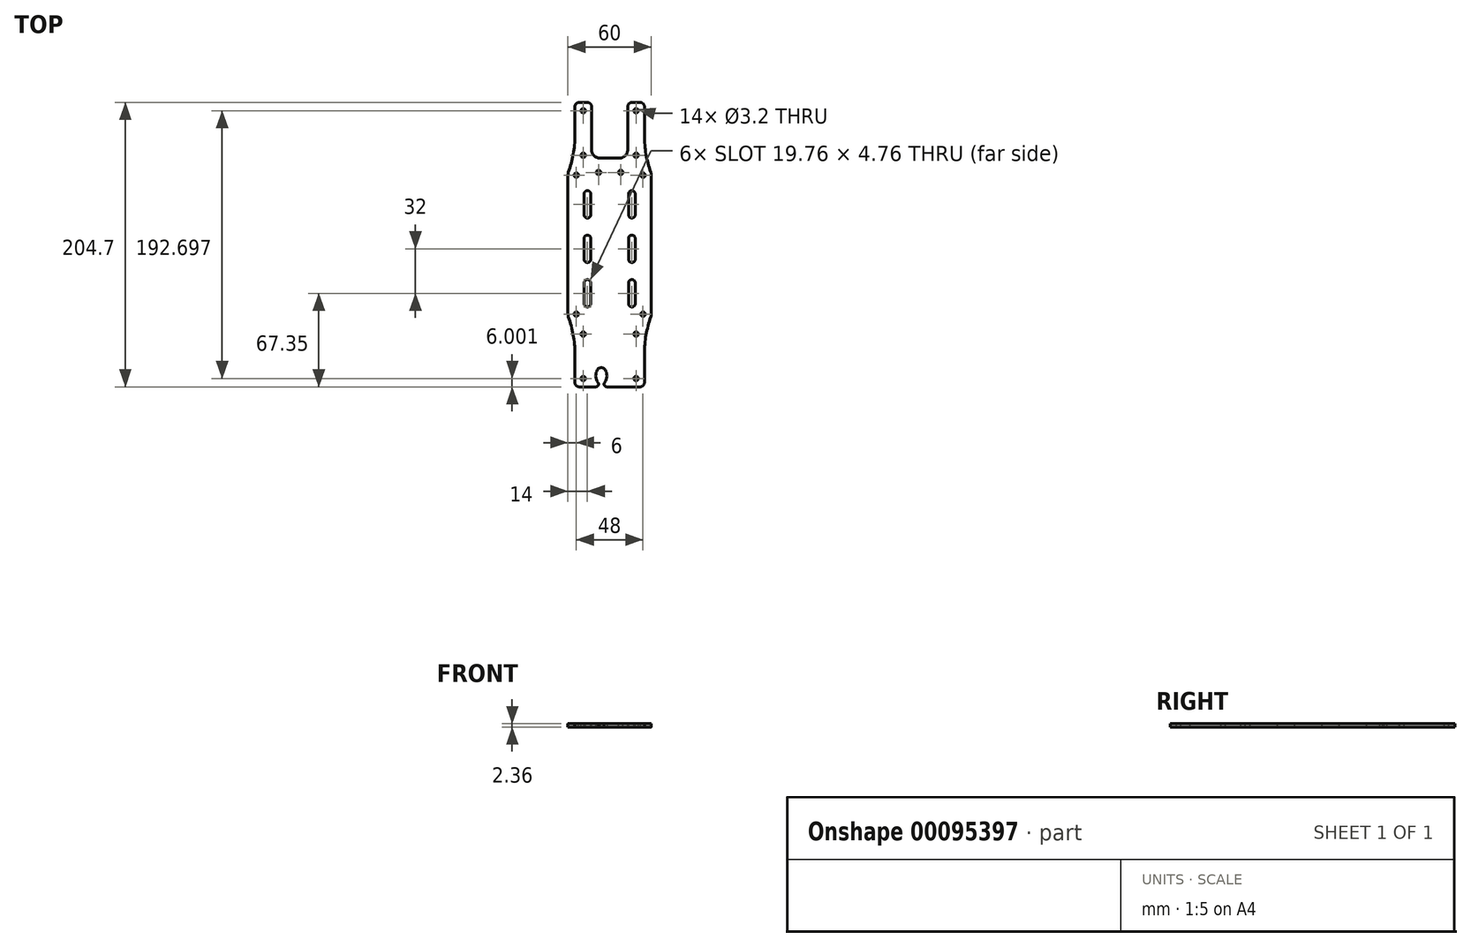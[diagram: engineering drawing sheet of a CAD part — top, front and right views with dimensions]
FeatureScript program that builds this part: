
annotation { "Feature Type Name" : "Feature", "Feature Type Description" : "" }
export const myFeature = defineFeature(function(context is Context, id is Id, definition is map)
    precondition{}
    {
        {
            var Q0;
            Q0=qCreatedBy(makeId("Top.planeOp"),FACE);
            var sketch = newSketch(context, id + "F0", { "sketchPlane" : qUnion([Q0])});
            skLineSegment(sketch, "E0", {"start": v(0, 102.35) * mm, "end": v(-22, 102.35) * mm});
            skLineSegment(sketch, "E1", {"start": v(-25, 99.35) * mm, "end": v(-25, 78.35) * mm});
            skLineSegment(sketch, "E2", {"start": v(-22, -102.35) * mm, "end": v(0, -102.35) * mm});
            skArc(sketch, "E3.filletArc", {"start": v(-22, 102.35) * mm, "mid": v(-24.12, 101.47) * mm, "end": v(-25, 99.35) * mm});
            skArc(sketch, "E4.filletArc", {"start": v(-25, -99.35) * mm, "mid": v(-24.12, -101.47) * mm, "end": v(-22, -102.35) * mm});
            skArc(sketch, "E5.filletArc", {"start": v(-29.64, 52.05) * mm, "mid": v(-29.9, 51.04) * mm, "end": v(-30, 50) * mm});
            skArc(sketch, "E6.MirrorCS", {"start": v(-29.64, -52.05) * mm, "mid": v(-29.9, -51.04) * mm, "end": v(-30, -50) * mm});
            skLineSegment(sketch, "E7.trimOffspring", {"start": v(-25, -78.35) * mm, "end": v(-25, -99.35) * mm});
            skArc(sketch, "E8", {"start": v(-25, -78.35) * mm, "mid": v(-26.17, -65) * mm, "end": v(-29.64, -52.05) * mm});
            skArc(sketch, "E9", {"start": v(-29.64, 52.05) * mm, "mid": v(-26.17, 65) * mm, "end": v(-25, 78.35) * mm});
            skCircle(sketch, "E10", {"center": v(0, 0) * mm, "radius": 125 * mm, "construction": true});
            skLineSegment(sketch, "E11", {"start": v(-95.76, 80.35) * mm, "end": v(95.76, -80.35) * mm, "construction": true});
            skLineSegment(sketch, "E12", {"start": v(95.76, 80.35) * mm, "end": v(-95.76, -80.35) * mm, "construction": true});
            skLineSegment(sketch, "E13", {"start": v(0, 125) * mm, "end": v(0, -125) * mm, "construction": true});
            skLineSegment(sketch, "E14", {"start": v(-95.76, 80.35) * mm, "end": v(95.76, 80.35) * mm, "construction": true});
            skLineSegment(sketch, "E15", {"start": v(-95.76, -80.35) * mm, "end": v(95.76, -80.35) * mm, "construction": true});
            skLineSegment(sketch, "E16", {"start": v(-30, 50) * mm, "end": v(-30, -50) * mm});
            skLineSegment(sketch, "E17.MirrorCS", {"start": v(0, 102.35) * mm, "end": v(22, 102.35) * mm});
            skArc(sketch, "E18.MirrorCS", {"start": v(22, 102.35) * mm, "mid": v(24.12, 101.47) * mm, "end": v(25, 99.35) * mm});
            skLineSegment(sketch, "E19.MirrorCS", {"start": v(25, 99.35) * mm, "end": v(25, 78.35) * mm});
            skArc(sketch, "E20.MirrorCS", {"start": v(29.64, 52.05) * mm, "mid": v(26.17, 65) * mm, "end": v(25, 78.35) * mm});
            skArc(sketch, "E21.MirrorCS", {"start": v(29.64, 52.05) * mm, "mid": v(29.9, 51.04) * mm, "end": v(30, 50) * mm});
            skLineSegment(sketch, "E22.MirrorCS", {"start": v(30, 50) * mm, "end": v(30, -50) * mm});
            skArc(sketch, "E23.MirrorCS", {"start": v(29.64, -52.05) * mm, "mid": v(29.9, -51.04) * mm, "end": v(30, -50) * mm});
            skArc(sketch, "E24.MirrorCS", {"start": v(25, -78.35) * mm, "mid": v(26.17, -65) * mm, "end": v(29.64, -52.05) * mm});
            skArc(sketch, "E25.MirrorCS", {"start": v(25, -99.35) * mm, "mid": v(24.12, -101.47) * mm, "end": v(22, -102.35) * mm});
            skLineSegment(sketch, "E26.MirrorCS", {"start": v(22, -102.35) * mm, "end": v(0, -102.35) * mm});
            skLineSegment(sketch, "E27.MirrorCS", {"start": v(25, -78.35) * mm, "end": v(25, -99.35) * mm});
            skSolve(sketch);
        }
        {
            var Q0;
            Q0=qSketchRegion(id+"F0",true);
            extrude(context, id + "F1", {"entities" : qUnion([Q0]), "oppositeDirection" : true, "depth" : 2.36 * mm});
        }
        {
            var Q0;
            Q0=makeQuery(id+"F1.opExtrude","CAP_FACE",FACE,{"disambiguationData":[OSD([sQuery(id+"F0.wireOp",EDGE,"E0"),sQuery(id+"F0.wireOp",EDGE,"E1"),sQuery(id+"F0.wireOp",EDGE,"E2"),sQuery(id+"F0.wireOp",EDGE,"E3.filletArc"),sQuery(id+"F0.wireOp",EDGE,"E4.filletArc"),sQuery(id+"F0.wireOp",EDGE,"d22b67ea-32aa-4b1a-bfbd-94ae52c1f5b30.MirrorCS"),sQuery(id+"F0.wireOp",EDGE,"d22b67ea-32aa-4b1a-bfbd-94ae52c1f5b31.MirrorCS"),sQuery(id+"F0.wireOp",EDGE,"d22b67ea-32aa-4b1a-bfbd-94ae52c1f5b32.MirrorCS"),sQuery(id+"F0.wireOp",EDGE,"d22b67ea-32aa-4b1a-bfbd-94ae52c1f5b33.MirrorCS"),sQuery(id+"F0.wireOp",EDGE,"d22b67ea-32aa-4b1a-bfbd-94ae52c1f5b34.MirrorCS")])],"isStart":true});
            var sketch = newSketch(context, id + "F2", { "sketchPlane" : qUnion([Q0])});
            skCircle(sketch, "E28", {"center": v(-19, 96.35) * mm, "radius": 1.6 * mm});
            skCircle(sketch, "E29", {"center": v(-19, 64.35) * mm, "radius": 1.6 * mm});
            skCircle(sketch, "E30", {"center": v(-19, -96.35) * mm, "radius": 1.6 * mm});
            skCircle(sketch, "E31", {"center": v(-19, -64.35) * mm, "radius": 1.6 * mm});
            skCircle(sketch, "E32", {"center": v(-24, -50) * mm, "radius": 1.6 * mm});
            skCircle(sketch, "E33", {"center": v(-24, 50) * mm, "radius": 1.6 * mm});
            skLineSegment(sketch, "E34", {"start": v(-19, 96.35) * mm, "end": v(-19, -96.35) * mm, "construction": true});
            skCircle(sketch, "E35.MirrorC", {"center": v(19, 96.35) * mm, "radius": 1.6 * mm});
            skCircle(sketch, "E36.MirrorC", {"center": v(19, 64.35) * mm, "radius": 1.6 * mm});
            skCircle(sketch, "E37.MirrorC", {"center": v(24, 50) * mm, "radius": 1.6 * mm});
            skCircle(sketch, "E38.MirrorC", {"center": v(24, -50) * mm, "radius": 1.6 * mm});
            skCircle(sketch, "E39.MirrorC", {"center": v(19, -64.35) * mm, "radius": 1.6 * mm});
            skCircle(sketch, "E40.MirrorC", {"center": v(19, -96.35) * mm, "radius": 1.6 * mm});
            skLineSegment(sketch, "E41", {"start": v(0, 0) * mm, "end": v(-30, 0) * mm, "construction": true});
            skLineSegment(sketch, "E42.left", {"start": v(-13.62, -42.5) * mm, "end": v(-13.62, -27.5) * mm});
            skLineSegment(sketch, "E42.right", {"start": v(-18.38, -42.5) * mm, "end": v(-18.38, -27.5) * mm});
            skPoint(sketch, "E42.middle", {"position": v(-16, -35) * mm});
            skArc(sketch, "E43", {"start": v(-13.62, -27.5) * mm, "mid": v(-16, -25.12) * mm, "end": v(-18.38, -27.5) * mm});
            skArc(sketch, "E44", {"start": v(-18.38, -42.5) * mm, "mid": v(-16, -44.88) * mm, "end": v(-13.62, -42.5) * mm});
            skArc(sketch, "E45.0.1.0", {"start": v(-18.38, -10.5) * mm, "mid": v(-16, -12.88) * mm, "end": v(-13.62, -10.5) * mm});
            skLineSegment(sketch, "E45.0.1.1", {"start": v(-18.38, -10.5) * mm, "end": v(-18.38, 4.5) * mm});
            skArc(sketch, "E45.0.1.2", {"start": v(-13.62, 4.5) * mm, "mid": v(-16, 6.88) * mm, "end": v(-18.38, 4.5) * mm});
            skLineSegment(sketch, "E45.0.1.3", {"start": v(-13.62, -10.5) * mm, "end": v(-13.62, 4.5) * mm});
            skArc(sketch, "E45.0.2.0", {"start": v(-18.38, 21.5) * mm, "mid": v(-16, 19.12) * mm, "end": v(-13.62, 21.5) * mm});
            skLineSegment(sketch, "E45.0.2.1", {"start": v(-18.38, 21.5) * mm, "end": v(-18.38, 36.5) * mm});
            skArc(sketch, "E45.0.2.2", {"start": v(-13.62, 36.5) * mm, "mid": v(-16, 38.88) * mm, "end": v(-18.38, 36.5) * mm});
            skLineSegment(sketch, "E45.0.2.3", {"start": v(-13.62, 21.5) * mm, "end": v(-13.62, 36.5) * mm});
            skArc(sketch, "E45.1.0.0", {"start": v(13.62, -42.5) * mm, "mid": v(16, -44.88) * mm, "end": v(18.38, -42.5) * mm});
            skLineSegment(sketch, "E45.1.0.1", {"start": v(13.62, -42.5) * mm, "end": v(13.62, -27.5) * mm});
            skArc(sketch, "E45.1.0.2", {"start": v(18.38, -27.5) * mm, "mid": v(16, -25.12) * mm, "end": v(13.62, -27.5) * mm});
            skLineSegment(sketch, "E45.1.0.3", {"start": v(18.38, -42.5) * mm, "end": v(18.38, -27.5) * mm});
            skArc(sketch, "E45.1.1.0", {"start": v(13.62, -10.5) * mm, "mid": v(16, -12.88) * mm, "end": v(18.38, -10.5) * mm});
            skLineSegment(sketch, "E45.1.1.1", {"start": v(13.62, -10.5) * mm, "end": v(13.62, 4.5) * mm});
            skArc(sketch, "E45.1.1.2", {"start": v(18.38, 4.5) * mm, "mid": v(16, 6.88) * mm, "end": v(13.62, 4.5) * mm});
            skLineSegment(sketch, "E45.1.1.3", {"start": v(18.38, -10.5) * mm, "end": v(18.38, 4.5) * mm});
            skArc(sketch, "E45.1.2.0", {"start": v(13.62, 21.5) * mm, "mid": v(16, 19.12) * mm, "end": v(18.38, 21.5) * mm});
            skLineSegment(sketch, "E45.1.2.1", {"start": v(13.62, 21.5) * mm, "end": v(13.62, 36.5) * mm});
            skArc(sketch, "E45.1.2.2", {"start": v(18.38, 36.5) * mm, "mid": v(16, 38.88) * mm, "end": v(13.62, 36.5) * mm});
            skLineSegment(sketch, "E45.1.2.3", {"start": v(18.38, 21.5) * mm, "end": v(18.38, 36.5) * mm});
            skLineSegment(sketch, "E45.direction1", {"start": v(-18.38, -42.5) * mm, "end": v(13.62, -42.5) * mm, "construction": true});
            skLineSegment(sketch, "E45.direction2", {"start": v(-18.38, -42.5) * mm, "end": v(-18.38, -10.5) * mm, "construction": true});
            skLineSegment(sketch, "E46", {"start": v(-8, 52) * mm, "end": v(8, 52) * mm, "construction": true});
            skPoint(sketch, "E47", {"position": v(0, 52) * mm});
            skCircle(sketch, "E48", {"center": v(-8, 52) * mm, "radius": 1.6 * mm});
            skCircle(sketch, "E49", {"center": v(8, 52) * mm, "radius": 1.6 * mm});
            skSolve(sketch);
        }
        {
            var Q0;
            Q0=qSketchRegion(id+"F2",true);
            extrude(context, id + "F3", {"entities" : qUnion([Q0]), "operationType" : NewBodyOperationType.REMOVE, "endBound" : BoundingType.THROUGH_ALL, "oppositeDirection" : true, "depth" : 25.4 * mm});
        }
        {
            var Q0;
            Q0=qCreatedBy(makeId("Top.planeOp"),FACE);
            var sketch = newSketch(context, id + "F4", { "sketchPlane" : qUnion([Q0])});
            skCircle(sketch, "E50.cCircle", {"center": v(-24, 50) * mm, "radius": 3.1 * mm, "construction": true});
            skLineSegment(sketch, "E50.0", {"start": v(-24, 53.58) * mm, "end": v(-20.9, 51.79) * mm, "construction": true});
            skLineSegment(sketch, "E50.1", {"start": v(-20.9, 51.79) * mm, "end": v(-20.9, 48.21) * mm, "construction": true});
            skLineSegment(sketch, "E50.2", {"start": v(-20.9, 48.21) * mm, "end": v(-24, 46.42) * mm, "construction": true});
            skLineSegment(sketch, "E50.3", {"start": v(-24, 46.42) * mm, "end": v(-27.1, 48.21) * mm, "construction": true});
            skLineSegment(sketch, "E50.4", {"start": v(-27.1, 48.21) * mm, "end": v(-27.1, 51.79) * mm, "construction": true});
            skLineSegment(sketch, "E50.5", {"start": v(-27.1, 51.79) * mm, "end": v(-24, 53.58) * mm, "construction": true});
            skPoint(sketch, "E50.0.midPoint", {"position": v(-22.45, 52.68) * mm});
            skArc(sketch, "E51", {"start": v(-20, 45.53) * mm, "mid": v(-24, 56) * mm, "end": v(-28, 45.53) * mm});
            skArc(sketch, "E52", {"start": v(-28, -45.53) * mm, "mid": v(-24, -56) * mm, "end": v(-20, -45.53) * mm});
            skLineSegment(sketch, "E53", {"start": v(-26, 41.06) * mm, "end": v(-26, -41.06) * mm});
            skLineSegment(sketch, "E54", {"start": v(-22, 41.06) * mm, "end": v(-22, -41.06) * mm});
            skPoint(sketch, "E55.visualSharp", {"position": v(-26, 44.34) * mm});
            skArc(sketch, "E55.filletArc", {"start": v(-26, 41.06) * mm, "mid": v(-26.52, 43.5) * mm, "end": v(-28, 45.53) * mm});
            skPoint(sketch, "E56.visualSharp", {"position": v(-22, 44.34) * mm});
            skArc(sketch, "E56.filletArc", {"start": v(-20, 45.53) * mm, "mid": v(-21.48, 43.5) * mm, "end": v(-22, 41.06) * mm});
            skPoint(sketch, "E57.visualSharp", {"position": v(-22, -44.34) * mm});
            skArc(sketch, "E57.filletArc", {"start": v(-22, -41.06) * mm, "mid": v(-21.48, -43.5) * mm, "end": v(-20, -45.53) * mm});
            skPoint(sketch, "E58.visualSharp", {"position": v(-26, -44.34) * mm});
            skArc(sketch, "E58.filletArc", {"start": v(-28, -45.53) * mm, "mid": v(-26.52, -43.5) * mm, "end": v(-26, -41.06) * mm});
            skLineSegment(sketch, "E59", {"start": v(-24, 50) * mm, "end": v(-24, -50) * mm, "construction": true});
            skSolve(sketch);
        }
        {
            var Q0;
            Q0=qSketchRegion(id+"F4",true);
            extrude(context, id + "F5", {"entities" : qUnion([Q0]), "depth" : 25 * mm});
        }
        {
            var Q0;
            Q0=makeQuery(id+"F5.opExtrude","CAP_FACE",FACE,{"disambiguationData":[OSD([sQuery(id+"F4.wireOp",EDGE,"E51"),sQuery(id+"F4.wireOp",EDGE,"E52"),sQuery(id+"F4.wireOp",EDGE,"E53"),sQuery(id+"F4.wireOp",EDGE,"E54"),sQuery(id+"F4.wireOp",EDGE,"E55.filletArc"),sQuery(id+"F4.wireOp",EDGE,"E56.filletArc"),sQuery(id+"F4.wireOp",EDGE,"E57.filletArc"),sQuery(id+"F4.wireOp",EDGE,"E58.filletArc")])],"isStart":true});
            var sketch = newSketch(context, id + "F6", { "sketchPlane" : qUnion([Q0])});
            skCircle(sketch, "E60.cCircle", {"center": v(-24, -50) * mm, "radius": 3.05 * mm, "construction": true});
            skLineSegment(sketch, "E60.0", {"start": v(-27.05, -48.24) * mm, "end": v(-24, -46.48) * mm});
            skLineSegment(sketch, "E60.1", {"start": v(-24, -46.48) * mm, "end": v(-20.95, -48.24) * mm});
            skLineSegment(sketch, "E60.2", {"start": v(-20.95, -48.24) * mm, "end": v(-20.95, -51.76) * mm});
            skLineSegment(sketch, "E60.3", {"start": v(-20.95, -51.76) * mm, "end": v(-24, -53.52) * mm});
            skLineSegment(sketch, "E60.4", {"start": v(-24, -53.52) * mm, "end": v(-27.05, -51.76) * mm});
            skLineSegment(sketch, "E60.5", {"start": v(-27.05, -51.76) * mm, "end": v(-27.05, -48.24) * mm});
            skPoint(sketch, "E60.0.midPoint", {"position": v(-25.53, -47.36) * mm});
            skCircle(sketch, "E61.cCircle", {"center": v(-24, 50) * mm, "radius": 3.05 * mm, "construction": true});
            skLineSegment(sketch, "E61.0", {"start": v(-27.05, 51.76) * mm, "end": v(-24, 53.52) * mm});
            skLineSegment(sketch, "E61.1", {"start": v(-24, 53.52) * mm, "end": v(-20.95, 51.76) * mm});
            skLineSegment(sketch, "E61.2", {"start": v(-20.95, 51.76) * mm, "end": v(-20.95, 48.24) * mm});
            skLineSegment(sketch, "E61.3", {"start": v(-20.95, 48.24) * mm, "end": v(-24, 46.48) * mm});
            skLineSegment(sketch, "E61.4", {"start": v(-24, 46.48) * mm, "end": v(-27.05, 48.24) * mm});
            skLineSegment(sketch, "E61.5", {"start": v(-27.05, 48.24) * mm, "end": v(-27.05, 51.76) * mm});
            skPoint(sketch, "E61.0.midPoint", {"position": v(-25.52, 52.64) * mm});
            skSolve(sketch);
        }
        {
            var Q0;
            Q0=qSketchRegion(id+"F6",true);
            var Q1;
            Q1=makeQuery(id+"F5.opExtrude","CAP_FACE",FACE,{"disambiguationData":[OSD([sQuery(id+"F4.wireOp",EDGE,"E51"),sQuery(id+"F4.wireOp",EDGE,"E52"),sQuery(id+"F4.wireOp",EDGE,"E53"),sQuery(id+"F4.wireOp",EDGE,"E54"),sQuery(id+"F4.wireOp",EDGE,"E55.filletArc"),sQuery(id+"F4.wireOp",EDGE,"E56.filletArc"),sQuery(id+"F4.wireOp",EDGE,"E57.filletArc"),sQuery(id+"F4.wireOp",EDGE,"E58.filletArc")])],"isStart":false});
            extrude(context, id + "F7", {"entities" : qUnion([Q0]), "operationType" : NewBodyOperationType.REMOVE, "endBound" : BoundingType.UP_TO_SURFACE, "oppositeDirection" : true, "endBoundEntityFace" : qUnion([Q1]), "depth" : 25 * mm});
        }
        {
            var Q0;
            Q0=makeQuery(id+"F5.opExtrude","SWEPT_FACE",FACE,{"disambiguationData":[OSD([sQuery(id+"F4.wireOp",EDGE,"E53")])]});
            var sketch = newSketch(context, id + "F8", { "sketchPlane" : qUnion([Q0])});
            skLineSegment(sketch, "E62", {"start": v(-21.13, 12.5) * mm, "end": v(21.13, 12.5) * mm, "construction": true});
            skLineSegment(sketch, "E63.bottom", {"start": v(-11.25, 17.5) * mm, "end": v(-19.25, 17.5) * mm});
            skLineSegment(sketch, "E63.top", {"start": v(-11.25, 7.5) * mm, "end": v(-19.25, 7.5) * mm});
            skLineSegment(sketch, "E63.left", {"start": v(-10.25, 16.5) * mm, "end": v(-10.25, 8.5) * mm});
            skLineSegment(sketch, "E63.right", {"start": v(-20.25, 16.5) * mm, "end": v(-20.25, 8.5) * mm});
            skPoint(sketch, "E63.middle", {"position": v(-15.25, 12.5) * mm});
            skPoint(sketch, "E64.visualSharp", {"position": v(-20.25, 17.5) * mm});
            skArc(sketch, "E64.filletArc", {"start": v(-19.25, 17.5) * mm, "mid": v(-19.96, 17.2) * mm, "end": v(-20.25, 16.5) * mm});
            skPoint(sketch, "E65.visualSharp", {"position": v(-20.25, 7.5) * mm});
            skArc(sketch, "E65.filletArc", {"start": v(-20.25, 8.5) * mm, "mid": v(-19.96, 7.8) * mm, "end": v(-19.25, 7.5) * mm});
            skPoint(sketch, "E66.visualSharp", {"position": v(-10.25, 7.5) * mm});
            skArc(sketch, "E66.filletArc", {"start": v(-11.25, 7.5) * mm, "mid": v(-10.54, 7.8) * mm, "end": v(-10.25, 8.5) * mm});
            skPoint(sketch, "E67.visualSharp", {"position": v(-10.25, 17.5) * mm});
            skArc(sketch, "E67.filletArc", {"start": v(-10.25, 16.5) * mm, "mid": v(-10.54, 17.2) * mm, "end": v(-11.25, 17.5) * mm});
            skLineSegment(sketch, "E68.bottom", {"start": v(-7.5, 0) * mm, "end": v(7.5, 0) * mm});
            skLineSegment(sketch, "E68.top", {"start": v(-6.5, 3.5) * mm, "end": v(6.5, 3.5) * mm});
            skLineSegment(sketch, "E68.left", {"start": v(-7.5, 0) * mm, "end": v(-7.5, 2.5) * mm});
            skLineSegment(sketch, "E68.right", {"start": v(7.5, 0) * mm, "end": v(7.5, 2.5) * mm});
            skPoint(sketch, "E69.visualSharp", {"position": v(-7.5, 3.5) * mm});
            skArc(sketch, "E69.filletArc", {"start": v(-6.5, 3.5) * mm, "mid": v(-7.2, 3.2) * mm, "end": v(-7.5, 2.5) * mm});
            skPoint(sketch, "E70.visualSharp", {"position": v(7.5, 3.5) * mm});
            skArc(sketch, "E70.filletArc", {"start": v(7.5, 2.5) * mm, "mid": v(7.2, 3.2) * mm, "end": v(6.5, 3.5) * mm});
            skArc(sketch, "E71", {"start": v(-27, 25) * mm, "mid": v(-25, 23) * mm, "end": v(-23, 25) * mm});
            skLineSegment(sketch, "E72", {"start": v(-25, 25) * mm, "end": v(-25, 0) * mm, "construction": true});
            skArc(sketch, "E73", {"start": v(-23, 0) * mm, "mid": v(-25, 2) * mm, "end": v(-27, 0) * mm});
            skLineSegment(sketch, "E74", {"start": v(-27, 25) * mm, "end": v(-23, 25) * mm});
            skLineSegment(sketch, "E75", {"start": v(-27, 0) * mm, "end": v(-23, 0) * mm});
            skLineSegment(sketch, "E76", {"start": v(0, 25) * mm, "end": v(0, 0) * mm, "construction": true});
            skPoint(sketch, "E77", {"position": v(0, 12.5) * mm});
            skArc(sketch, "E78.MirrorCS", {"start": v(11.25, 7.5) * mm, "mid": v(10.54, 7.8) * mm, "end": v(10.25, 8.5) * mm});
            skArc(sketch, "E79.MirrorCS", {"start": v(10.25, 16.5) * mm, "mid": v(10.54, 17.2) * mm, "end": v(11.25, 17.5) * mm});
            skArc(sketch, "E80.MirrorCS", {"start": v(20.25, 8.5) * mm, "mid": v(19.96, 7.8) * mm, "end": v(19.25, 7.5) * mm});
            skArc(sketch, "E81.MirrorCS", {"start": v(19.25, 17.5) * mm, "mid": v(19.96, 17.2) * mm, "end": v(20.25, 16.5) * mm});
            skPoint(sketch, "E82.MirrorP", {"position": v(10.25, 17.5) * mm});
            skLineSegment(sketch, "E83.MirrorCS", {"start": v(20.25, 16.5) * mm, "end": v(20.25, 8.5) * mm});
            skLineSegment(sketch, "E84.MirrorCS", {"start": v(10.25, 16.5) * mm, "end": v(10.25, 8.5) * mm});
            skLineSegment(sketch, "E85.MirrorCS", {"start": v(11.25, 17.5) * mm, "end": v(19.25, 17.5) * mm});
            skLineSegment(sketch, "E86.MirrorCS", {"start": v(11.25, 7.5) * mm, "end": v(19.25, 7.5) * mm});
            skPoint(sketch, "E87.MirrorP", {"position": v(20.25, 7.5) * mm});
            skPoint(sketch, "E88.MirrorP", {"position": v(15.25, 12.5) * mm});
            skPoint(sketch, "E89.MirrorP", {"position": v(20.25, 17.5) * mm});
            skPoint(sketch, "E90.MirrorP", {"position": v(10.25, 7.5) * mm});
            skLineSegment(sketch, "E91.MirrorCS", {"start": v(27, 25) * mm, "end": v(23, 25) * mm});
            skLineSegment(sketch, "E92.MirrorCS", {"start": v(25, 25) * mm, "end": v(25, 0) * mm, "construction": true});
            skArc(sketch, "E93.MirrorCS", {"start": v(27, 25) * mm, "mid": v(25, 23) * mm, "end": v(23, 25) * mm});
            skLineSegment(sketch, "E94.MirrorCS", {"start": v(27, 0) * mm, "end": v(23, 0) * mm});
            skArc(sketch, "E95.MirrorCS", {"start": v(23, 0) * mm, "mid": v(25, 2) * mm, "end": v(27, 0) * mm});
            skArc(sketch, "E96.MirrorCS", {"start": v(-6.5, 21.5) * mm, "mid": v(-7.2, 21.8) * mm, "end": v(-7.5, 22.5) * mm});
            skArc(sketch, "E97.MirrorCS", {"start": v(7.5, 22.5) * mm, "mid": v(7.2, 21.8) * mm, "end": v(6.5, 21.5) * mm});
            skPoint(sketch, "E98.MirrorP", {"position": v(-7.5, 21.5) * mm});
            skLineSegment(sketch, "E99.MirrorCS", {"start": v(-6.5, 21.5) * mm, "end": v(6.5, 21.5) * mm});
            skLineSegment(sketch, "E100.MirrorCS", {"start": v(-7.5, 25) * mm, "end": v(-7.5, 22.5) * mm});
            skPoint(sketch, "E101.MirrorP", {"position": v(7.5, 21.5) * mm});
            skLineSegment(sketch, "E102.MirrorCS", {"start": v(7.5, 25) * mm, "end": v(7.5, 22.5) * mm});
            skLineSegment(sketch, "E103.MirrorCS", {"start": v(-7.5, 25) * mm, "end": v(7.5, 25) * mm});
            skSolve(sketch);
        }
        {
            var Q0;
            Q0=qSketchRegion(id+"F8",true);
            var Q1;
            Q1=makeQuery(id+"F5.opExtrude","SWEPT_FACE",FACE,{"disambiguationData":[OSD([sQuery(id+"F4.wireOp",EDGE,"E54")])]});
            extrude(context, id + "F9", {"entities" : qUnion([Q0]), "operationType" : NewBodyOperationType.REMOVE, "endBound" : BoundingType.UP_TO_SURFACE, "oppositeDirection" : true, "endBoundEntityFace" : qUnion([Q1]), "depth" : 25 * mm});
        }
        {
            var Q0;
            Q0=qCreatedBy(makeId("Top.planeOp"),FACE);
            cPlane(context, id + "F10", {"entities" : qUnion([Q0]), "cplaneType" : CPlaneType.OFFSET, "offset" : 12.5 * mm, "width" : 150 * mm, "height" : 150 * mm});
        }
        {
            var Q0;
            Q0=qCreatedBy(id+"F10.planeOp",FACE);
            var sketch = newSketch(context, id + "F11", { "sketchPlane" : qUnion([Q0])});
            skLineSegment(sketch, "E104", {"start": v(-26.25, 21.25) * mm, "end": v(-26.25, 19.75) * mm});
            skLineSegment(sketch, "E105", {"start": v(-25.75, 19.25) * mm, "end": v(-19.25, 19.25) * mm});
            skLineSegment(sketch, "E106", {"start": v(-19.25, 19.25) * mm, "end": v(-18.25, 18.25) * mm});
            skLineSegment(sketch, "E107", {"start": v(-18.25, 18.25) * mm, "end": v(-15.25, 18.25) * mm});
            skLineSegment(sketch, "E108", {"start": v(-6.48, 15.25) * mm, "end": v(-35.06, 15.25) * mm, "construction": true});
            skArc(sketch, "E109", {"start": v(-12.25, 15.25) * mm, "mid": v(-13.13, 17.37) * mm, "end": v(-15.25, 18.25) * mm});
            skLineSegment(sketch, "E110", {"start": v(-26.25, 21.25) * mm, "end": v(-27.75, 21.25) * mm});
            skLineSegment(sketch, "E111", {"start": v(-27.75, 21.25) * mm, "end": v(-27.75, 15.25) * mm});
            skPoint(sketch, "E112.visualSharp", {"position": v(-26.25, 19.25) * mm});
            skArc(sketch, "E112.filletArc", {"start": v(-26.25, 19.75) * mm, "mid": v(-26.1, 19.4) * mm, "end": v(-25.75, 19.25) * mm});
            skLineSegment(sketch, "E113.MirrorCS", {"start": v(-27.75, 9.25) * mm, "end": v(-27.75, 15.25) * mm});
            skLineSegment(sketch, "E114.MirrorCS", {"start": v(-26.25, 9.25) * mm, "end": v(-27.75, 9.25) * mm});
            skLineSegment(sketch, "E115.MirrorCS", {"start": v(-26.25, 9.25) * mm, "end": v(-26.25, 10.75) * mm});
            skArc(sketch, "E116.MirrorCS", {"start": v(-26.25, 10.75) * mm, "mid": v(-26.1, 11.1) * mm, "end": v(-25.75, 11.25) * mm});
            skLineSegment(sketch, "E117.MirrorCS", {"start": v(-25.75, 11.25) * mm, "end": v(-19.25, 11.25) * mm});
            skLineSegment(sketch, "E118.MirrorCS", {"start": v(-19.25, 11.25) * mm, "end": v(-18.25, 12.25) * mm});
            skLineSegment(sketch, "E119.MirrorCS", {"start": v(-18.25, 12.25) * mm, "end": v(-15.25, 12.25) * mm});
            skArc(sketch, "E120.MirrorCS", {"start": v(-12.25, 15.25) * mm, "mid": v(-13.13, 13.13) * mm, "end": v(-15.25, 12.25) * mm});
            skSolve(sketch);
        }
        {
            var Q0;
            Q0=qSketchRegion(id+"F11",true);
            extrude(context, id + "F12", {"entities" : qUnion([Q0]), "endBound" : BoundingType.SYMMETRIC, "depth" : 8 * mm});
        }
        {
            var Q0;
            Q0=makeQuery(id+"F12.opExtrude","CAP_FACE",FACE,{"disambiguationData":[OSD([sQuery(id+"F11.wireOp",EDGE,"E104"),sQuery(id+"F11.wireOp",EDGE,"E105"),sQuery(id+"F11.wireOp",EDGE,"E106"),sQuery(id+"F11.wireOp",EDGE,"E107"),sQuery(id+"F11.wireOp",EDGE,"E109"),sQuery(id+"F11.wireOp",EDGE,"E110"),sQuery(id+"F11.wireOp",EDGE,"E111"),sQuery(id+"F11.wireOp",EDGE,"E112.filletArc"),sQuery(id+"F11.wireOp",EDGE,"E113.MirrorCS"),sQuery(id+"F11.wireOp",EDGE,"E114.MirrorCS"),sQuery(id+"F11.wireOp",EDGE,"E115.MirrorCS"),sQuery(id+"F11.wireOp",EDGE,"E116.MirrorCS"),sQuery(id+"F11.wireOp",EDGE,"E117.MirrorCS"),sQuery(id+"F11.wireOp",EDGE,"E118.MirrorCS"),sQuery(id+"F11.wireOp",EDGE,"E119.MirrorCS"),sQuery(id+"F11.wireOp",EDGE,"E120.MirrorCS")])],"isStart":false});
            var sketch = newSketch(context, id + "F13", { "sketchPlane" : qUnion([Q0])});
            skCircle(sketch, "E121", {"center": v(-15.25, 15.25) * mm, "radius": 1.5 * mm});
            skSolve(sketch);
        }
        {
            var Q0;
            Q0=qSketchRegion(id+"F13",true);
            var Q1;
            Q1=makeQuery(id+"F12.opExtrude","CAP_FACE",FACE,{"disambiguationData":[OSD([sQuery(id+"F11.wireOp",EDGE,"E104"),sQuery(id+"F11.wireOp",EDGE,"E105"),sQuery(id+"F11.wireOp",EDGE,"E106"),sQuery(id+"F11.wireOp",EDGE,"E107"),sQuery(id+"F11.wireOp",EDGE,"E109"),sQuery(id+"F11.wireOp",EDGE,"E110"),sQuery(id+"F11.wireOp",EDGE,"E111"),sQuery(id+"F11.wireOp",EDGE,"E112.filletArc"),sQuery(id+"F11.wireOp",EDGE,"E113.MirrorCS"),sQuery(id+"F11.wireOp",EDGE,"E114.MirrorCS"),sQuery(id+"F11.wireOp",EDGE,"E115.MirrorCS"),sQuery(id+"F11.wireOp",EDGE,"E116.MirrorCS"),sQuery(id+"F11.wireOp",EDGE,"E117.MirrorCS"),sQuery(id+"F11.wireOp",EDGE,"E118.MirrorCS"),sQuery(id+"F11.wireOp",EDGE,"E119.MirrorCS"),sQuery(id+"F11.wireOp",EDGE,"E120.MirrorCS")])],"isStart":true});
            extrude(context, id + "F14", {"entities" : qUnion([Q0]), "operationType" : NewBodyOperationType.REMOVE, "endBound" : BoundingType.UP_TO_SURFACE, "oppositeDirection" : true, "endBoundEntityFace" : qUnion([Q1]), "depth" : 25 * mm});
        }
        {
            var Q0;
            Q0=makeQuery(id+"F5.opExtrude","SWEPT_BODY",BODY,{"disambiguationData":[OSD([sQuery(id+"F4.wireOp",EDGE,"E51"),sQuery(id+"F4.wireOp",EDGE,"E52"),sQuery(id+"F4.wireOp",EDGE,"E53"),sQuery(id+"F4.wireOp",EDGE,"E54"),sQuery(id+"F4.wireOp",EDGE,"E55.filletArc"),sQuery(id+"F4.wireOp",EDGE,"E56.filletArc"),sQuery(id+"F4.wireOp",EDGE,"E57.filletArc"),sQuery(id+"F4.wireOp",EDGE,"E58.filletArc")])]});
            deleteBodies(context, id + "F15", {"entities" : qUnion([Q0])});
        }
        {
            var Q0;
            Q0=makeQuery(id+"F12.opExtrude","SWEPT_BODY",BODY,{"disambiguationData":[OSD([sQuery(id+"F11.wireOp",EDGE,"E104"),sQuery(id+"F11.wireOp",EDGE,"E105"),sQuery(id+"F11.wireOp",EDGE,"E106"),sQuery(id+"F11.wireOp",EDGE,"E107"),sQuery(id+"F11.wireOp",EDGE,"E109"),sQuery(id+"F11.wireOp",EDGE,"E110"),sQuery(id+"F11.wireOp",EDGE,"E111"),sQuery(id+"F11.wireOp",EDGE,"E112.filletArc"),sQuery(id+"F11.wireOp",EDGE,"E113.MirrorCS"),sQuery(id+"F11.wireOp",EDGE,"E114.MirrorCS"),sQuery(id+"F11.wireOp",EDGE,"E115.MirrorCS"),sQuery(id+"F11.wireOp",EDGE,"E116.MirrorCS"),sQuery(id+"F11.wireOp",EDGE,"E117.MirrorCS"),sQuery(id+"F11.wireOp",EDGE,"E118.MirrorCS"),sQuery(id+"F11.wireOp",EDGE,"E119.MirrorCS"),sQuery(id+"F11.wireOp",EDGE,"E120.MirrorCS")])]});
            deleteBodies(context, id + "F16", {"entities" : qUnion([Q0])});
        }
        {
            var Q0;
            Q0=makeQuery(id+"F0.imprint","IMPRINT",FACE,{"disambiguationData":[TD([[makeQuery(id+"F0.imprint","IMPRINT",EDGE,{"derivedFrom":sQuery(id+"F0.wireOp",EDGE,"E0")}),1.0]])]});
            var sketch = newSketch(context, id + "F17", { "sketchPlane" : qUnion([Q0])});
            skLineSegment(sketch, "E122", {"start": v(0, 62.35) * mm, "end": v(-7, 62.35) * mm});
            skLineSegment(sketch, "E123", {"start": v(-13, 68.35) * mm, "end": v(-13, 99.35) * mm});
            skLineSegment(sketch, "E124", {"start": v(-16, 102.35) * mm, "end": v(-16, 102.35) * mm});
            skLineSegment(sketch, "E125", {"start": v(-16, 102.35) * mm, "end": v(-16, 105.35) * mm});
            skLineSegment(sketch, "E126", {"start": v(-16, 105.35) * mm, "end": v(0, 105.35) * mm});
            skPoint(sketch, "E127.visualSharp", {"position": v(-13, 62.35) * mm});
            skArc(sketch, "E127.filletArc", {"start": v(-13, 68.35) * mm, "mid": v(-11.24, 64.1) * mm, "end": v(-7, 62.35) * mm});
            skPoint(sketch, "E128.visualSharp", {"position": v(-13, 102.35) * mm});
            skArc(sketch, "E128.filletArc", {"start": v(-13, 99.35) * mm, "mid": v(-13.88, 101.47) * mm, "end": v(-16, 102.35) * mm});
            skLineSegment(sketch, "E129.MirrorCS", {"start": v(16, 102.35) * mm, "end": v(16, 105.35) * mm});
            skArc(sketch, "E130.MirrorCS", {"start": v(13, 99.35) * mm, "mid": v(13.88, 101.47) * mm, "end": v(16, 102.35) * mm});
            skArc(sketch, "E131.MirrorCS", {"start": v(13, 68.35) * mm, "mid": v(11.24, 64.1) * mm, "end": v(7, 62.35) * mm});
            skPoint(sketch, "E132.MirrorP", {"position": v(13, 102.35) * mm});
            skPoint(sketch, "E133.MirrorP", {"position": v(13, 62.35) * mm});
            skLineSegment(sketch, "E134.MirrorCS", {"start": v(16, 105.35) * mm, "end": v(0, 105.35) * mm});
            skLineSegment(sketch, "E135.MirrorCS", {"start": v(0, 62.35) * mm, "end": v(7, 62.35) * mm});
            skLineSegment(sketch, "E136.MirrorCS", {"start": v(13, 68.35) * mm, "end": v(13, 99.35) * mm});
            skSolve(sketch);
        }
        {
            var Q0;
            Q0 = qSketchRegion(id + "F17", true);
            var Q1;
            Q1=makeQuery(id+"F1.opExtrude","CAP_FACE",FACE,{"disambiguationData":[OSD([sQuery(id+"F0.wireOp",EDGE,"E0"),sQuery(id+"F0.wireOp",EDGE,"E1"),sQuery(id+"F0.wireOp",EDGE,"E2"),sQuery(id+"F0.wireOp",EDGE,"E3.filletArc"),sQuery(id+"F0.wireOp",EDGE,"E4.filletArc"),sQuery(id+"F0.wireOp",EDGE,"E5.filletArc"),sQuery(id+"F0.wireOp",EDGE,"E6.MirrorCS"),sQuery(id+"F0.wireOp",EDGE,"E7.trimOffspring"),sQuery(id+"F0.wireOp",EDGE,"E8"),sQuery(id+"F0.wireOp",EDGE,"E9"),sQuery(id+"F0.wireOp",EDGE,"E16"),sQuery(id+"F0.wireOp",EDGE,"E17.MirrorCS"),sQuery(id+"F0.wireOp",EDGE,"E18.MirrorCS"),sQuery(id+"F0.wireOp",EDGE,"E19.MirrorCS"),sQuery(id+"F0.wireOp",EDGE,"E20.MirrorCS"),sQuery(id+"F0.wireOp",EDGE,"E21.MirrorCS"),sQuery(id+"F0.wireOp",EDGE,"E22.MirrorCS"),sQuery(id+"F0.wireOp",EDGE,"E23.MirrorCS"),sQuery(id+"F0.wireOp",EDGE,"E24.MirrorCS"),sQuery(id+"F0.wireOp",EDGE,"E25.MirrorCS"),sQuery(id+"F0.wireOp",EDGE,"E26.MirrorCS"),sQuery(id+"F0.wireOp",EDGE,"E27.MirrorCS")])],"isStart":false});
            extrude(context, id + "F18", {"entities" : qUnion([Q0]), "operationType" : NewBodyOperationType.REMOVE, "endBound" : BoundingType.UP_TO_SURFACE, "oppositeDirection" : true, "endBoundEntityFace" : qUnion([Q1]), "depth" : 25 * mm});
        }
        {
            var Q0;
            Q0=makeQuery(id+"F1.opExtrude","CAP_FACE",FACE,{"disambiguationData":[OSD([sQuery(id+"F0.wireOp",EDGE,"E0"),sQuery(id+"F0.wireOp",EDGE,"E1"),sQuery(id+"F0.wireOp",EDGE,"E2"),sQuery(id+"F0.wireOp",EDGE,"E3.filletArc"),sQuery(id+"F0.wireOp",EDGE,"E4.filletArc"),sQuery(id+"F0.wireOp",EDGE,"E5.filletArc"),sQuery(id+"F0.wireOp",EDGE,"E6.MirrorCS"),sQuery(id+"F0.wireOp",EDGE,"E7.trimOffspring"),sQuery(id+"F0.wireOp",EDGE,"E8"),sQuery(id+"F0.wireOp",EDGE,"E9"),sQuery(id+"F0.wireOp",EDGE,"E16"),sQuery(id+"F0.wireOp",EDGE,"E17.MirrorCS"),sQuery(id+"F0.wireOp",EDGE,"E18.MirrorCS"),sQuery(id+"F0.wireOp",EDGE,"E19.MirrorCS"),sQuery(id+"F0.wireOp",EDGE,"E20.MirrorCS"),sQuery(id+"F0.wireOp",EDGE,"E21.MirrorCS"),sQuery(id+"F0.wireOp",EDGE,"E22.MirrorCS"),sQuery(id+"F0.wireOp",EDGE,"E23.MirrorCS"),sQuery(id+"F0.wireOp",EDGE,"E24.MirrorCS"),sQuery(id+"F0.wireOp",EDGE,"E25.MirrorCS"),sQuery(id+"F0.wireOp",EDGE,"E26.MirrorCS"),sQuery(id+"F0.wireOp",EDGE,"E27.MirrorCS")])],"isStart":true});
            var sketch = newSketch(context, id + "F19", { "sketchPlane" : qUnion([Q0])});
            skEllipticalArc(sketch, "E137", {});
            skArc(sketch, "E138", {"start": v(-10, -102.35) * mm, "mid": v(-8.19, -101.2) * mm, "end": v(-8.48, -99.06) * mm});
            skLineSegment(sketch, "E139", {"start": v(-6, -94.35) * mm, "end": v(-6, -104.97) * mm, "construction": true});
            skArc(sketch, "E140.MirrorCS", {"start": v(-2, -102.35) * mm, "mid": v(-3.81, -101.2) * mm, "end": v(-3.52, -99.06) * mm});
            skLineSegment(sketch, "E141", {"start": v(-10, -102.35) * mm, "end": v(-10, -103.35) * mm});
            skLineSegment(sketch, "E142", {"start": v(-10, -103.35) * mm, "end": v(-2, -103.35) * mm});
            skLineSegment(sketch, "E143", {"start": v(-2, -103.35) * mm, "end": v(-2, -102.35) * mm});
            const initialGuessF19  = {"E137": [-0.006, -0.09434845121081742, 0, 1, 0.006, 0.004, 3.808895997013649, 2.474289310165937]};
            skSetInitialGuess(sketch, initialGuessF19);
            skSolve(sketch);
        }
        {
            var Q0;
            Q0 = qSketchRegion(id + "F19", true);
            var Q1;
            Q1=makeQuery(id+"F1.opExtrude","CAP_FACE",FACE,{"disambiguationData":[OSD([sQuery(id+"F0.wireOp",EDGE,"E0"),sQuery(id+"F0.wireOp",EDGE,"E1"),sQuery(id+"F0.wireOp",EDGE,"E2"),sQuery(id+"F0.wireOp",EDGE,"E3.filletArc"),sQuery(id+"F0.wireOp",EDGE,"E4.filletArc"),sQuery(id+"F0.wireOp",EDGE,"E5.filletArc"),sQuery(id+"F0.wireOp",EDGE,"E6.MirrorCS"),sQuery(id+"F0.wireOp",EDGE,"E7.trimOffspring"),sQuery(id+"F0.wireOp",EDGE,"E8"),sQuery(id+"F0.wireOp",EDGE,"E9"),sQuery(id+"F0.wireOp",EDGE,"E16"),sQuery(id+"F0.wireOp",EDGE,"E17.MirrorCS"),sQuery(id+"F0.wireOp",EDGE,"E18.MirrorCS"),sQuery(id+"F0.wireOp",EDGE,"E19.MirrorCS"),sQuery(id+"F0.wireOp",EDGE,"E20.MirrorCS"),sQuery(id+"F0.wireOp",EDGE,"E21.MirrorCS"),sQuery(id+"F0.wireOp",EDGE,"E22.MirrorCS"),sQuery(id+"F0.wireOp",EDGE,"E23.MirrorCS"),sQuery(id+"F0.wireOp",EDGE,"E24.MirrorCS"),sQuery(id+"F0.wireOp",EDGE,"E25.MirrorCS"),sQuery(id+"F0.wireOp",EDGE,"E26.MirrorCS"),sQuery(id+"F0.wireOp",EDGE,"E27.MirrorCS")])],"isStart":false});
            extrude(context, id + "F20", {"entities" : qUnion([Q0]), "operationType" : NewBodyOperationType.REMOVE, "endBound" : BoundingType.UP_TO_SURFACE, "oppositeDirection" : true, "endBoundEntityFace" : qUnion([Q1]), "depth" : 25 * mm});
        }
    });
